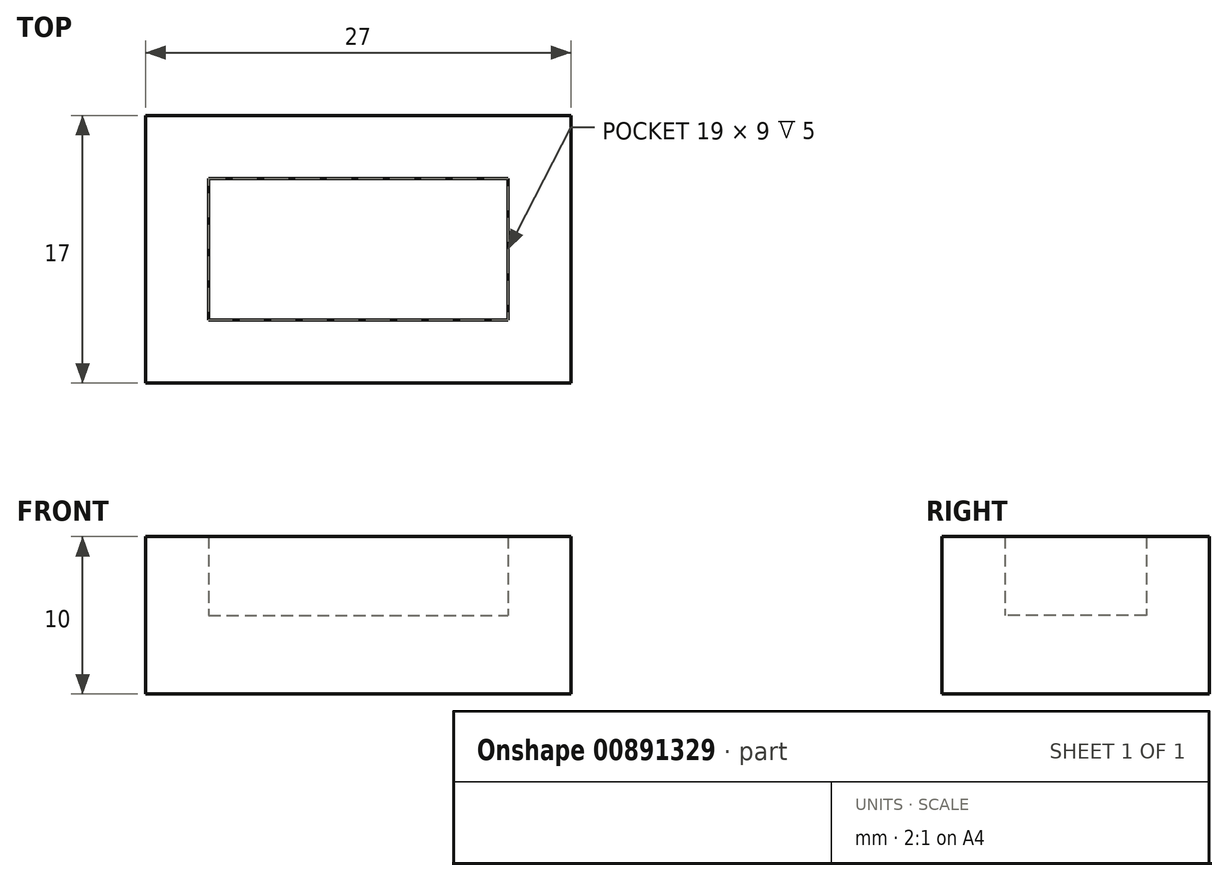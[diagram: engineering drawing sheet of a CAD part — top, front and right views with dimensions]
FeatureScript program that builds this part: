
annotation { "Feature Type Name" : "Feature", "Feature Type Description" : "" }
export const myFeature = defineFeature(function(context is Context, id is Id, definition is map)
    precondition{}
    {
        {
            var Q0;
            Q0=qCreatedBy(makeId("Top.planeOp"),FACE);
            var sketch = newSketch(context, id + "F0", { "sketchPlane" : qUnion([Q0])});
            skLineSegment(sketch, "E0", {"start": v(0, 0) * mm, "end": v(19, 0) * mm});
            skLineSegment(sketch, "E1", {"start": v(19, 0) * mm, "end": v(19, 9) * mm});
            skLineSegment(sketch, "E2", {"start": v(19, 9) * mm, "end": v(0, 9) * mm});
            skLineSegment(sketch, "E3", {"start": v(0, 9) * mm, "end": v(0, 0) * mm});
            skLineSegment(sketch, "E4", {"start": v(19, 0) * mm, "end": v(23, 0) * mm});
            skLineSegment(sketch, "E5", {"start": v(23, 0) * mm, "end": v(23, 13) * mm});
            skLineSegment(sketch, "E6", {"start": v(23, 13) * mm, "end": v(-4, 13) * mm});
            skLineSegment(sketch, "E7", {"start": v(-4, 13) * mm, "end": v(-4, -4) * mm});
            skLineSegment(sketch, "E8", {"start": v(-4, -4) * mm, "end": v(23, -4) * mm});
            skLineSegment(sketch, "E9", {"start": v(23, -4) * mm, "end": v(23, 0) * mm});
            skSolve(sketch);
        }
        {
            var Q0;
            Q0=makeQuery(id+"F0.imprint","IMPRINT",FACE,{"disambiguationData":[TD([[makeQuery(id+"F0.imprint","IMPRINT",EDGE,{"derivedFrom":sQuery(id+"F0.wireOp",EDGE,"E0")}),1.0]])]});
            var Q1;
            Q1=makeQuery(id+"F0.imprint","IMPRINT",FACE,{"disambiguationData":[TD([[makeQuery(id+"F0.imprint","IMPRINT",EDGE,{"derivedFrom":sQuery(id+"F0.wireOp",EDGE,"E0")}),-1.0]])]});
            extrude(context, id + "F1", {"entities" : qUnion([Q0, Q1]), "oppositeDirection" : true, "depth" : 5 * mm, "offsetDistance" : 25 * mm});
        }
        {
            var Q0;
            Q0=makeQuery(id+"F0.imprint","IMPRINT",FACE,{"disambiguationData":[TD([[makeQuery(id+"F0.imprint","IMPRINT",EDGE,{"derivedFrom":sQuery(id+"F0.wireOp",EDGE,"E0")}),-1.0]])]});
            extrude(context, id + "F2", {"entities" : qUnion([Q0]), "operationType" : NewBodyOperationType.ADD, "depth" : 5 * mm, "offsetDistance" : 25 * mm});
        }
    });
